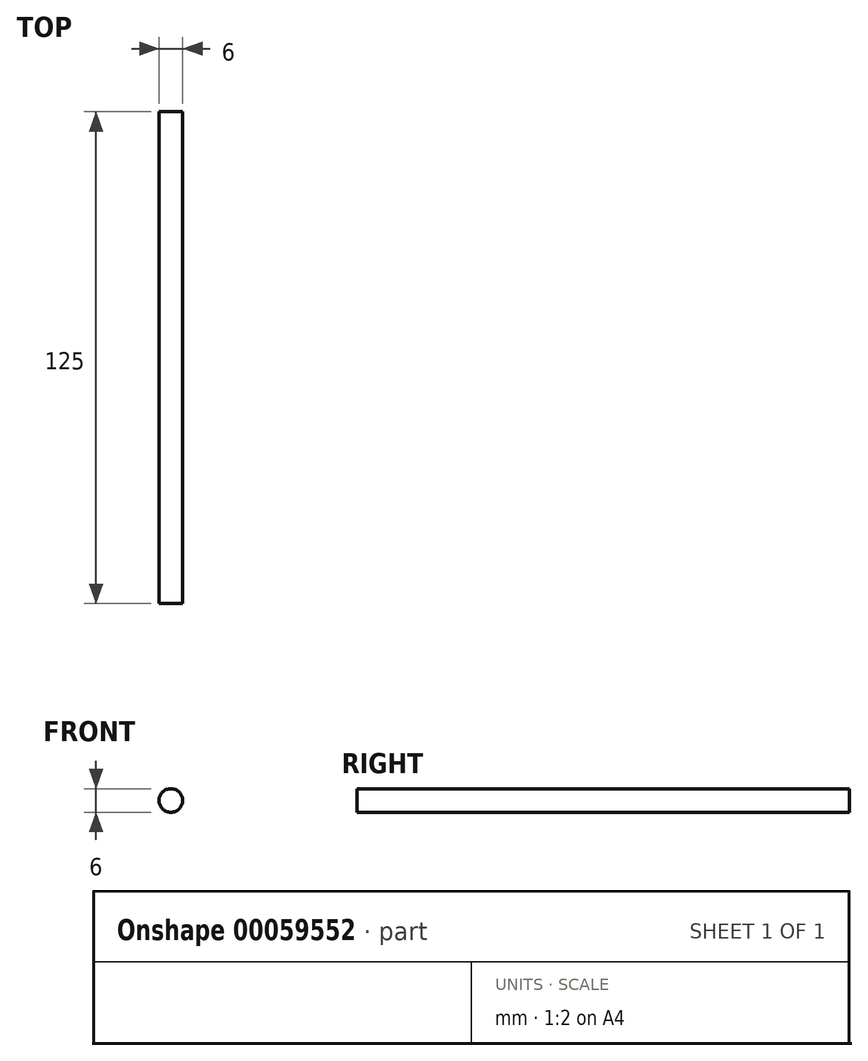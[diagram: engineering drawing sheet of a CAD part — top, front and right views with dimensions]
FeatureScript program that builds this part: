
annotation { "Feature Type Name" : "Feature", "Feature Type Description" : "" }
export const myFeature = defineFeature(function(context is Context, id is Id, definition is map)
    precondition{}
    {
        {
            var Q0;
            Q0=qCreatedBy(makeId("Front.planeOp"),FACE);
            var sketch = newSketch(context, id + "F0", { "sketchPlane" : qUnion([Q0])});
            skCircle(sketch, "E0", {"center": v(0, 0) * mm, "radius": 3 * mm});
            skSolve(sketch);
        }
        {
            var Q0;
            Q0 = qSketchRegion(id + "F0", true);
            extrude(context, id + "F1", {"entities" : qUnion([Q0]), "depth" : 125 * mm});
        }
    });
